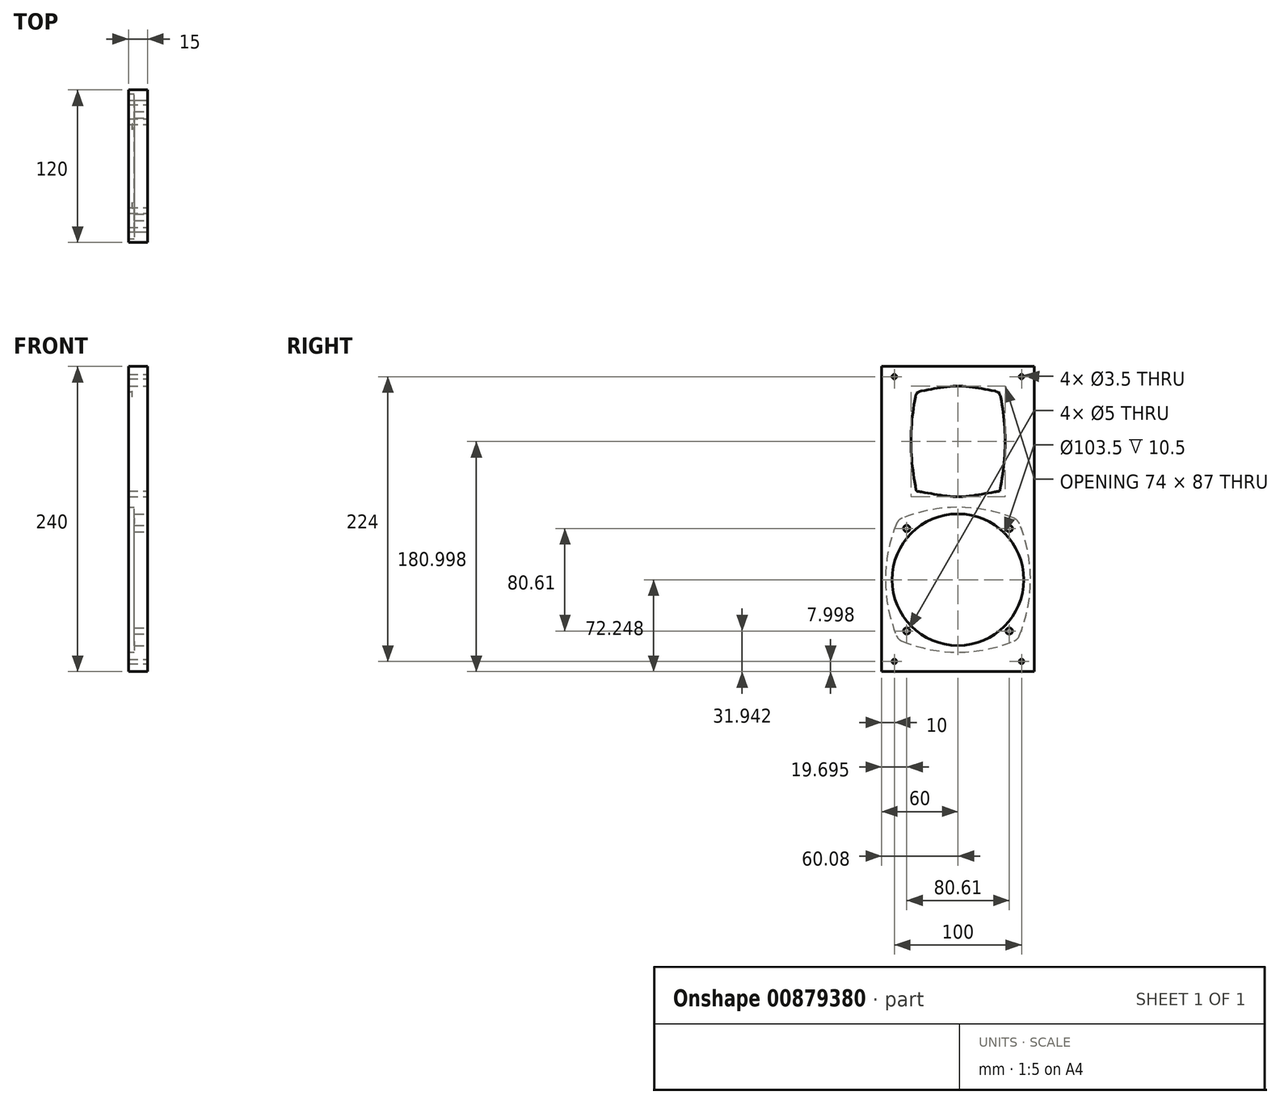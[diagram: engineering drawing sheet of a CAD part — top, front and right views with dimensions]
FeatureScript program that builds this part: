
annotation { "Feature Type Name" : "Feature", "Feature Type Description" : "" }
export const myFeature = defineFeature(function(context is Context, id is Id, definition is map)
    precondition{}
    {
        {
            var Q0;
            Q0=qCreatedBy(makeId("Right.planeOp"),FACE);
            var sketch = newSketch(context, id + "F0", { "sketchPlane" : qUnion([Q0])});
            skLineSegment(sketch, "E0.bottom", {"start": v(60, 118.4) * mm, "end": v(-60, 118.4) * mm});
            skLineSegment(sketch, "E1", {"start": v(60, -121.6) * mm, "end": v(-60, -121.6) * mm});
            skPoint(sketch, "E2", {"position": v(0, -49.34) * mm});
            skCircle(sketch, "E3", {"center": v(0, -49.34) * mm, "radius": 51.75 * mm});
            skCircle(sketch, "E4", {"center": v(40.3, -9.04) * mm, "radius": 2.5 * mm});
            skPoint(sketch, "E5", {"position": v(46.32, -3.03) * mm});
            skPoint(sketch, "E6", {"position": v(47.02, -2.32) * mm});
            skCircle(sketch, "E7.1.0", {"center": v(-40.3, -9.04) * mm, "radius": 2.5 * mm});
            skPoint(sketch, "E7.1.1", {"position": v(-46.32, -3.03) * mm});
            skPoint(sketch, "E7.1.2", {"position": v(-47.02, -2.32) * mm});
            skCircle(sketch, "E7.2.0", {"center": v(-40.3, -89.65) * mm, "radius": 2.5 * mm});
            skPoint(sketch, "E7.2.1", {"position": v(-46.32, -95.66) * mm});
            skPoint(sketch, "E7.2.2", {"position": v(-47.02, -96.37) * mm});
            skCircle(sketch, "E7.3.0", {"center": v(40.3, -89.65) * mm, "radius": 2.5 * mm});
            skPoint(sketch, "E7.3.1", {"position": v(46.32, -95.66) * mm});
            skPoint(sketch, "E7.3.2", {"position": v(47.02, -96.37) * mm});
            skPoint(sketch, "E8.1.0", {"position": v(-57, -49.34) * mm});
            skPoint(sketch, "E8.2.0", {"position": v(0, -106.34) * mm});
            skPoint(sketch, "E8.3.0", {"position": v(57, -49.34) * mm});
            skArc(sketch, "E9", {"start": v(43.97, -1.01) * mm, "mid": v(0, 7.66) * mm, "end": v(-43.97, -1.01) * mm});
            skArc(sketch, "E10", {"start": v(-48.33, -5.38) * mm, "mid": v(-57, -49.34) * mm, "end": v(-48.33, -93.3) * mm});
            skArc(sketch, "E11", {"start": v(-43.97, -97.67) * mm, "mid": v(0, -106.34) * mm, "end": v(43.97, -97.67) * mm});
            skArc(sketch, "E12", {"start": v(48.33, -93.3) * mm, "mid": v(57, -49.34) * mm, "end": v(48.33, -5.38) * mm});
            skLineSegment(sketch, "E13.trimOffspring", {"start": v(0, 9.4) * mm, "end": v(0, 9.45) * mm});
            skPoint(sketch, "E14.start.orphan", {"position": v(0, -113.34) * mm});
            skLineSegment(sketch, "E15.bottom", {"start": v(0.08, 90.9) * mm, "end": v(0, 90.9) * mm});
            skPoint(sketch, "E16", {"position": v(0.08, 102.9) * mm});
            skPoint(sketch, "E17", {"position": v(0.08, 15.9) * mm});
            skPoint(sketch, "E18", {"position": v(-36.92, 59.4) * mm});
            skPoint(sketch, "E19", {"position": v(37.08, 59.4) * mm});
            skPoint(sketch, "E20", {"position": v(29, 93.88) * mm});
            skLineSegment(sketch, "E21", {"start": v(0.08, 59.4) * mm, "end": v(0, 59.4) * mm});
            skLineSegment(sketch, "E22", {"start": v(0, 59.4) * mm, "end": v(0.08, 59.4) * mm});
            skPoint(sketch, "E23.MirrorP", {"position": v(29, 24.94) * mm});
            skPoint(sketch, "E24", {"position": v(32.86, 98.48) * mm});
            skPoint(sketch, "E25.MirrorP", {"position": v(-32.7, 98.48) * mm});
            skPoint(sketch, "E26.MirrorP", {"position": v(32.86, 20.34) * mm});
            skPoint(sketch, "E27.MirrorP", {"position": v(-32.7, 20.34) * mm});
            skFitSpline(sketch, "E28", {"points": [v(32.86, 98.48) * mm, v(0.08, 102.9) * mm, v(-32.7, 98.48) * mm], "startDerivative": vector(-65.56, 9.7) * mm, "endDerivative": vector(-65.56, -9.7) * mm});
            skFitSpline(sketch, "E29", {"points": [v(-32.7, 98.48) * mm, v(-36.92, 59.4) * mm, v(-32.7, 20.34) * mm], "startDerivative": vector(-15.65, -78.14) * mm, "endDerivative": vector(15.65, -78.14) * mm});
            skFitSpline(sketch, "E30", {"points": [v(-32.7, 20.34) * mm, v(0.08, 15.9) * mm, v(32.86, 20.34) * mm], "startDerivative": vector(65.56, -9.7) * mm, "endDerivative": vector(65.56, 9.7) * mm});
            skFitSpline(sketch, "E31", {"points": [v(32.86, 20.34) * mm, v(37.08, 59.4) * mm, v(32.86, 98.48) * mm], "startDerivative": vector(15.65, 78.14) * mm, "endDerivative": vector(-15.65, 78.14) * mm});
            skCircle(sketch, "E32", {"center": v(29, 93.88) * mm, "radius": 1.75 * mm});
            skCircle(sketch, "E33", {"center": v(-28.85, 93.88) * mm, "radius": 1.75 * mm});
            skCircle(sketch, "E34", {"center": v(29, 24.94) * mm, "radius": 1.75 * mm});
            skCircle(sketch, "E35", {"center": v(-28.85, 24.94) * mm, "radius": 1.75 * mm});
            skPoint(sketch, "E36.orphan", {"position": v(0.08, 59.4) * mm});
            skLineSegment(sketch, "E37.bottom", {"start": v(19.08, 98.4) * mm, "end": v(-18.92, 98.4) * mm});
            skLineSegment(sketch, "E37.top", {"start": v(19.08, 20.4) * mm, "end": v(-18.92, 20.4) * mm});
            skLineSegment(sketch, "E37.left", {"start": v(22.08, 95.4) * mm, "end": v(22.08, 23.4) * mm});
            skLineSegment(sketch, "E37.right", {"start": v(-21.92, 95.4) * mm, "end": v(-21.92, 23.4) * mm});
            skPoint(sketch, "E38.visualSharp", {"position": v(22.08, 98.4) * mm});
            skArc(sketch, "E38.filletArc", {"start": v(22.08, 95.4) * mm, "mid": v(21.2, 97.53) * mm, "end": v(19.08, 98.4) * mm});
            skPoint(sketch, "E39.visualSharp", {"position": v(-21.92, 98.4) * mm});
            skArc(sketch, "E39.filletArc", {"start": v(-18.92, 98.4) * mm, "mid": v(-21.04, 97.53) * mm, "end": v(-21.92, 95.4) * mm});
            skPoint(sketch, "E40.visualSharp", {"position": v(-21.92, 20.4) * mm});
            skArc(sketch, "E40.filletArc", {"start": v(-21.92, 23.4) * mm, "mid": v(-21.04, 21.29) * mm, "end": v(-18.92, 20.4) * mm});
            skPoint(sketch, "E41.visualSharp", {"position": v(22.08, 20.4) * mm});
            skArc(sketch, "E41.filletArc", {"start": v(19.08, 20.4) * mm, "mid": v(21.2, 21.29) * mm, "end": v(22.08, 23.4) * mm});
            skArc(sketch, "E42.filletArc", {"start": v(33.66, 94.3) * mm, "mid": v(31.98, 97.49) * mm, "end": v(28.77, 99.13) * mm});
            skArc(sketch, "E43.filletArc", {"start": v(-28.6, 99.13) * mm, "mid": v(-31.82, 97.49) * mm, "end": v(-33.5, 94.3) * mm});
            skArc(sketch, "E44.filletArc", {"start": v(-33.5, 24.52) * mm, "mid": v(-31.82, 21.33) * mm, "end": v(-28.6, 19.69) * mm});
            skArc(sketch, "E45.filletArc", {"start": v(28.77, 19.69) * mm, "mid": v(31.98, 21.33) * mm, "end": v(33.66, 24.52) * mm});
            skLineSegment(sketch, "E46", {"start": v(60, 118.4) * mm, "end": v(60, -121.6) * mm});
            skLineSegment(sketch, "E47", {"start": v(-60, 118.4) * mm, "end": v(-60, -121.6) * mm});
            skPoint(sketch, "E48.orphan", {"position": v(0, 118.4) * mm});
            skLineSegment(sketch, "E49.bottom", {"start": v(-60, 118.4) * mm, "end": v(60, 118.4) * mm});
            skLineSegment(sketch, "E49.top", {"start": v(-60, -121.6) * mm, "end": v(60, -121.6) * mm});
            skPoint(sketch, "E50.right.start.orphan", {"position": v(80.87, 118.4) * mm});
            skPoint(sketch, "E51.trimOffspring.end.orphan", {"position": v(0, -121.6) * mm});
            skCircle(sketch, "E52.0.1.0", {"center": v(-50, 110.4) * mm, "radius": 1.75 * mm});
            skCircle(sketch, "E53.0.1.0", {"center": v(50, 110.4) * mm, "radius": 1.75 * mm});
            skCircle(sketch, "E54.0.1.0", {"center": v(50, -113.6) * mm, "radius": 1.75 * mm});
            skCircle(sketch, "E55.0.1.0", {"center": v(-50, -113.6) * mm, "radius": 1.75 * mm});
            skArc(sketch, "E56.filletArc", {"start": v(48.33, -5.38) * mm, "mid": v(46.58, -2.76) * mm, "end": v(43.97, -1.01) * mm});
            skArc(sketch, "E57.filletArc", {"start": v(-43.97, -1.01) * mm, "mid": v(-46.58, -2.76) * mm, "end": v(-48.33, -5.38) * mm});
            skArc(sketch, "E58.filletArc", {"start": v(-48.33, -93.3) * mm, "mid": v(-46.58, -95.93) * mm, "end": v(-43.97, -97.67) * mm});
            skArc(sketch, "E59.filletArc", {"start": v(43.97, -97.67) * mm, "mid": v(46.58, -95.93) * mm, "end": v(48.33, -93.3) * mm});
            skSolve(sketch);
        }
        {
            var Q0;
            Q0=makeQuery(id+"F0.imprint","IMPRINT",FACE,{"disambiguationData":[TD([[makeQuery(id+"F0.imprint","IMPRINT",EDGE,{"derivedFrom":sQuery(id+"F0.wireOp",EDGE,"E9")}),-1.0]])]});
            extrude(context, id + "F1", {"entities" : qUnion([Q0]), "oppositeDirection" : true, "depth" : 15 * mm, "offsetDistance" : 25 * mm});
        }
        {
            var Q0;
            Q0=makeQuery(id+"F0.imprint","IMPRINT",FACE,{"disambiguationData":[TD([[makeQuery(id+"F0.imprint","IMPRINT",EDGE,{"derivedFrom":sQuery(id+"F0.wireOp",EDGE,"E28")}),1.0]])]});
            extrude(context, id + "F2", {"entities" : qUnion([Q0]), "operationType" : NewBodyOperationType.ADD, "oppositeDirection" : true, "depth" : 12 * mm, "offsetDistance" : 25 * mm});
        }
        {
            var Q0;
            Q0=makeQuery(id+"F0.imprint","IMPRINT",FACE,{"disambiguationData":[TD([[makeQuery(id+"F0.imprint","IMPRINT",EDGE,{"derivedFrom":sQuery(id+"F0.wireOp",EDGE,"E3")}),-1.0]])]});
            extrude(context, id + "F3", {"entities" : qUnion([Q0]), "operationType" : NewBodyOperationType.ADD, "oppositeDirection" : true, "depth" : 10.5 * mm, "offsetDistance" : 25 * mm});
        }
    });
